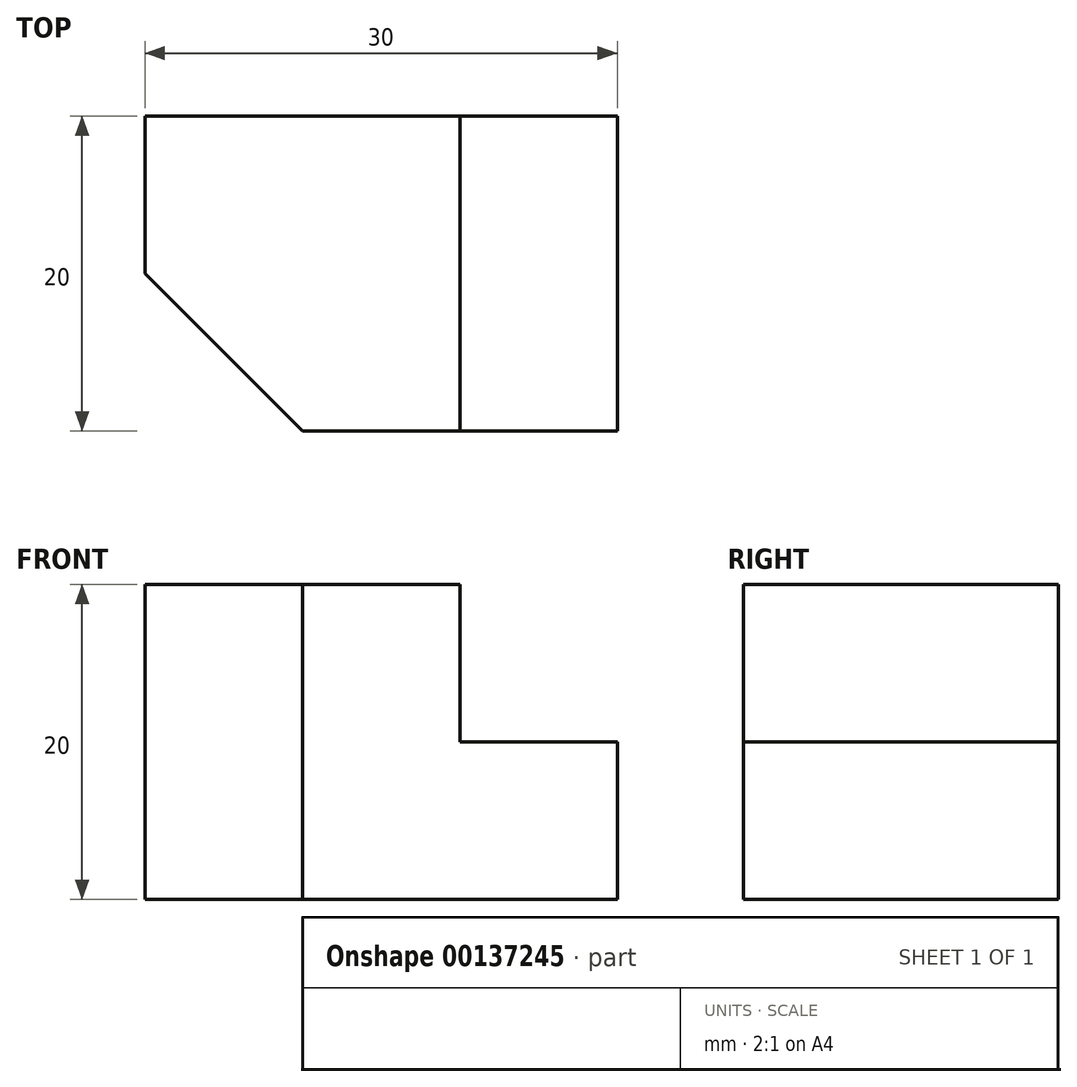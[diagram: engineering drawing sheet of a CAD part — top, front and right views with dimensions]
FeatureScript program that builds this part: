
annotation { "Feature Type Name" : "Feature", "Feature Type Description" : "" }
export const myFeature = defineFeature(function(context is Context, id is Id, definition is map)
    precondition{}
    {
        {
            var Q0;
            Q0=qCreatedBy(makeId("Top.planeOp"),FACE);
            var sketch = newSketch(context, id + "F0", { "sketchPlane" : qUnion([Q0])});
            skLineSegment(sketch, "E0", {"start": v(0, 10) * mm, "end": v(0, 20) * mm});
            skLineSegment(sketch, "E1", {"start": v(0, 20) * mm, "end": v(20, 20) * mm});
            skLineSegment(sketch, "E2", {"start": v(20, 20) * mm, "end": v(20, 0) * mm});
            skLineSegment(sketch, "E3", {"start": v(20, 0) * mm, "end": v(10, 0) * mm});
            skLineSegment(sketch, "E4", {"start": v(10, 0) * mm, "end": v(0, 10) * mm});
            skLineSegment(sketch, "E5", {"start": v(20, 20) * mm, "end": v(30, 20) * mm});
            skLineSegment(sketch, "E6", {"start": v(30, 20) * mm, "end": v(30, 0) * mm});
            skLineSegment(sketch, "E7", {"start": v(30, 0) * mm, "end": v(20, 0) * mm});
            skSolve(sketch);
        }
        {
            var Q0;
            Q0=makeQuery(id+"F0.imprint","IMPRINT",FACE,{"disambiguationData":[TD([[makeQuery(id+"F0.imprint","IMPRINT",EDGE,{"derivedFrom":sQuery(id+"F0.wireOp",EDGE,"E0")}),-1.0]])]});
            extrude(context, id + "F1", {"entities" : qUnion([Q0]), "depth" : 20 * mm});
        }
        {
            var Q0;
            Q0=makeQuery(id+"F0.imprint","IMPRINT",FACE,{"disambiguationData":[TD([[makeQuery(id+"F0.imprint","IMPRINT",EDGE,{"derivedFrom":sQuery(id+"F0.wireOp",EDGE,"E2")}),1.0]])]});
            extrude(context, id + "F2", {"entities" : qUnion([Q0]), "operationType" : NewBodyOperationType.ADD, "depth" : 10 * mm});
        }
    });
